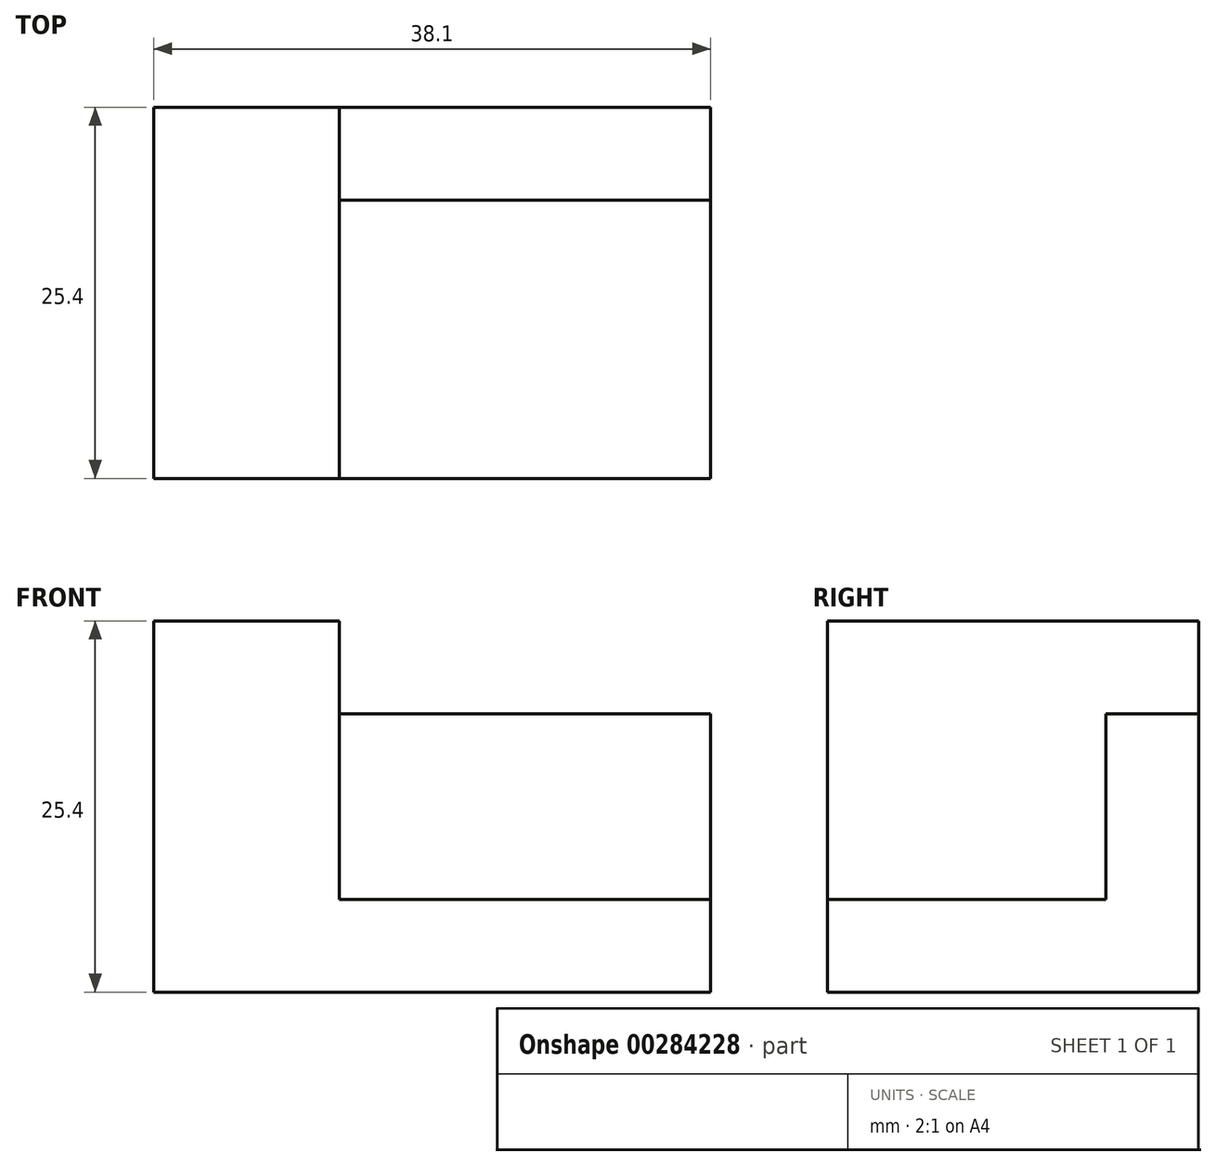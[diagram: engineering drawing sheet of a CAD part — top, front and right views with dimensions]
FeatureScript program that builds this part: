
annotation { "Feature Type Name" : "Feature", "Feature Type Description" : "" }
export const myFeature = defineFeature(function(context is Context, id is Id, definition is map)
    precondition{}
    {
        {
            var Q0;
            Q0=qCreatedBy(makeId("Front.planeOp"),FACE);
            var sketch = newSketch(context, id + "F0", { "sketchPlane" : qUnion([Q0])});
            skLineSegment(sketch, "E0", {"start": v(0, 0) * mm, "end": v(0, 25.4) * mm});
            skLineSegment(sketch, "E1", {"start": v(0, 25.4) * mm, "end": v(12.7, 25.4) * mm});
            skLineSegment(sketch, "E2", {"start": v(12.7, 25.4) * mm, "end": v(12.7, 19.05) * mm});
            skLineSegment(sketch, "E3", {"start": v(12.7, 19.05) * mm, "end": v(38.1, 19.05) * mm});
            skLineSegment(sketch, "E4", {"start": v(0, 0) * mm, "end": v(38.1, 0) * mm});
            skLineSegment(sketch, "E5", {"start": v(38.1, 19.05) * mm, "end": v(38.1, 0) * mm});
            skSolve(sketch);
        }
        {
            var Q0;
            Q0 = qSketchRegion(id + "F0", true);
            extrude(context, id + "F1", {"entities" : qUnion([Q0]), "depth" : 25.4 * mm});
        }
        {
            var Q0;
            Q0=makeQuery(id+"F1.opExtrude","CAP_FACE",FACE,{"disambiguationData":[OSD([sQuery(id+"F0.wireOp",EDGE,"E0"),sQuery(id+"F0.wireOp",EDGE,"E1"),sQuery(id+"F0.wireOp",EDGE,"E2"),sQuery(id+"F0.wireOp",EDGE,"E3"),sQuery(id+"F0.wireOp",EDGE,"E4"),sQuery(id+"F0.wireOp",EDGE,"E5")])],"isStart":false});
            var sketch = newSketch(context, id + "F2", { "sketchPlane" : qUnion([Q0])});
            skLineSegment(sketch, "E6.bottom", {"start": v(12.7, 19.05) * mm, "end": v(38.1, 19.05) * mm});
            skLineSegment(sketch, "E6.top", {"start": v(12.7, 6.35) * mm, "end": v(38.1, 6.35) * mm});
            skLineSegment(sketch, "E6.left", {"start": v(12.7, 19.05) * mm, "end": v(12.7, 6.35) * mm});
            skLineSegment(sketch, "E6.right", {"start": v(38.1, 19.05) * mm, "end": v(38.1, 6.35) * mm});
            skSolve(sketch);
        }
        {
            var Q0;
            Q0 = qSketchRegion(id + "F2", true);
            extrude(context, id + "F3", {"entities" : qUnion([Q0]), "operationType" : NewBodyOperationType.REMOVE, "oppositeDirection" : true, "depth" : 19.05 * mm});
        }
    });
